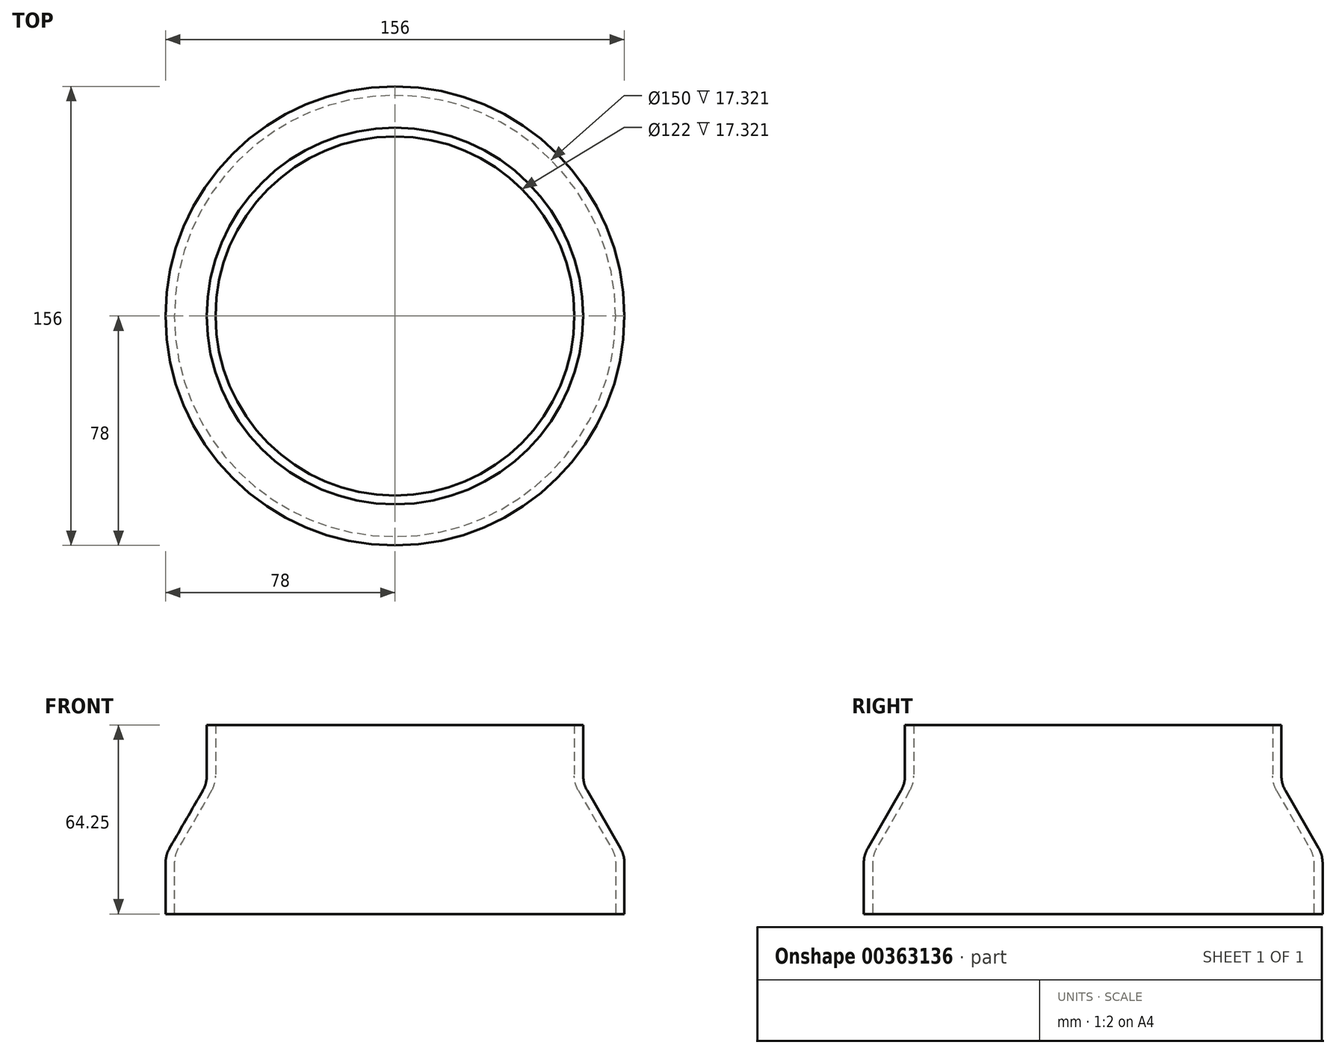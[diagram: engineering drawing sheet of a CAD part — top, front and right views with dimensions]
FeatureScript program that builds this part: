
annotation { "Feature Type Name" : "Feature", "Feature Type Description" : "" }
export const myFeature = defineFeature(function(context is Context, id is Id, definition is map)
    precondition{}
    {
        {
            var Q0;
            Q0=qCreatedBy(makeId("Front.planeOp"),FACE);
            var sketch = newSketch(context, id + "F0", { "sketchPlane" : qUnion([Q0])});
            skLineSegment(sketch, "E0", {"start": v(62.34, 8.17) * mm, "end": v(73.66, -11.44) * mm});
            skLineSegment(sketch, "E1", {"start": v(75, -16.44) * mm, "end": v(75, -33.76) * mm});
            skLineSegment(sketch, "E2", {"start": v(75, -33.76) * mm, "end": v(78, -33.76) * mm});
            skLineSegment(sketch, "E3", {"start": v(78, -33.76) * mm, "end": v(78, -16.44) * mm});
            skLineSegment(sketch, "E4", {"start": v(76.66, -11.44) * mm, "end": v(65.34, 8.17) * mm});
            skLineSegment(sketch, "E5", {"start": v(64, 10.49) * mm, "end": v(61, 10.49) * mm});
            skLineSegment(sketch, "E6", {"start": v(61, 13.17) * mm, "end": v(61, 30.49) * mm});
            skLineSegment(sketch, "E7", {"start": v(61, 30.49) * mm, "end": v(64, 30.49) * mm});
            skLineSegment(sketch, "E8", {"start": v(64, 30.49) * mm, "end": v(64, 13.17) * mm});
            skLineSegment(sketch, "E9", {"start": v(0, -80.8) * mm, "end": v(0, 86.88) * mm, "construction": true});
            skPoint(sketch, "E10.visualSharp", {"position": v(64, 10.49) * mm});
            skArc(sketch, "E10.filletArc", {"start": v(64, 13.17) * mm, "mid": v(64.34, 10.58) * mm, "end": v(65.34, 8.17) * mm});
            skPoint(sketch, "E11.visualSharp", {"position": v(78, -13.76) * mm});
            skArc(sketch, "E11.filletArc", {"start": v(78, -16.44) * mm, "mid": v(77.66, -13.85) * mm, "end": v(76.66, -11.44) * mm});
            skPoint(sketch, "E12.visualSharp", {"position": v(61, 10.49) * mm});
            skArc(sketch, "E12.filletArc", {"start": v(61, 13.17) * mm, "mid": v(61.34, 10.58) * mm, "end": v(62.34, 8.17) * mm});
            skPoint(sketch, "E13.visualSharp", {"position": v(75, -13.76) * mm});
            skArc(sketch, "E13.filletArc", {"start": v(75, -16.44) * mm, "mid": v(74.66, -13.85) * mm, "end": v(73.66, -11.44) * mm});
            skLineSegment(sketch, "E14", {"start": v(78, -16.53) * mm, "end": v(78, 4.98) * mm, "construction": true});
            skSolve(sketch);
        }
        {
            var Q0;
            Q0 = qSketchRegion(id + "F0", true);
            var Q1;
            Q1=sQuery(id+"F0.wireOp",EDGE,"E9");
            revolve(context, id + "F1", {"entities" : qUnion([Q0]), "axis" : qUnion([Q1]), "revolveType" : RevolveType.FULL});
        }
    });
